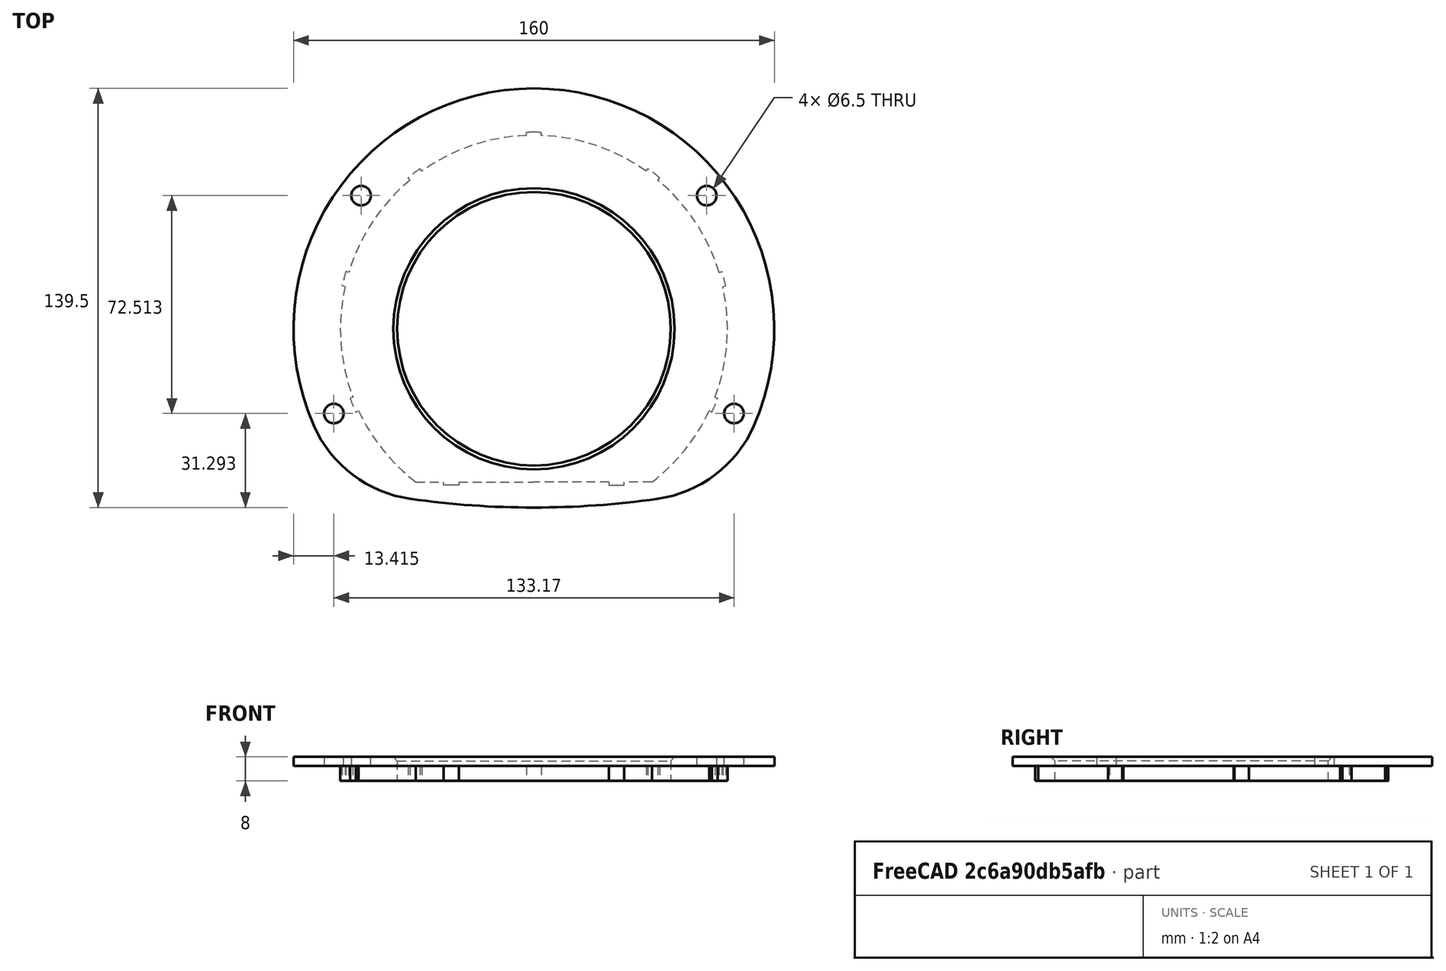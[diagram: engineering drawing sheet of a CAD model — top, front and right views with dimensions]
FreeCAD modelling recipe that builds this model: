
FCSTD DOCUMENT  (FreeCAD 0.20R29410 (Git))
Label: RevolverHole
License: All rights reserved
LicenseURL: http://en.wikipedia.org/wiki/All_rights_reserved
objects: Sketcher::SketchObject×3, PartDesign::Pad×2, Mesh::Feature×1, PartDesign::Pocket×1, PartDesign::Mirrored×1, PartDesign::Chamfer×1, PartDesign::Body×1
note: 13 computed .brp shape members not serialized (recipe doc carries the construction recipe); baked Part::Feature solids carry a one-line shape summary decoded from their .brp

FEATURE [Mesh::Feature] Revolver_Hole
FEATURE [Sketcher::SketchObject] Sketch
  FullyConstrained = true
  MapMode = 5
  Support = -> [XY_Plane]
  sketch-geometry (4):
    g0: ArcOfCircle CenterX=0 CenterY=233.5 CenterZ=0 NormalX=0 NormalY=0 NormalZ=1 AngleXU=0 Radius=293 StartAngle=4.71239 EndAngle=4.85294
    g1: ArcOfCircle CenterX=35.2333 CenterY=-15.5198 CenterZ=0 NormalX=0 NormalY=0 NormalZ=1 AngleXU=0 Radius=41.5 StartAngle=4.85294 EndAngle=5.86827
    g2: ArcOfCircle CenterX=0 CenterY=0 CenterZ=0 NormalX=0 NormalY=0 NormalZ=1 AngleXU=0 Radius=80 StartAngle=5.86827 EndAngle=7.85398
    g3: LineSegment StartX=2.45e-14 StartY=80 StartZ=0 EndX=-5.38e-14 EndY=-59.5 EndZ=0
  constraints (12):
    c: PointOnObject(g0,g-2)
    c: PointOnObject(g0,g-2)
    c: Coincident(g2,g-1)
    c: PointOnObject(g2,g-2)
    c: Coincident(g3,g2)
    c: Coincident(g3,g0)
    c: Tangent(g2,g1) = -1.5708
    c: Tangent(g1,g0) = -1.5708
    c: Diameter(g2) = 160
    c: Diameter(g0) = 586
    c: DistanceY(g0) = -59.5
    c: Diameter(g1) = 83
FEATURE [Sketcher::SketchObject] Sketch001
  FullyConstrained = true
  MapMode = 5
  Support = -> [XY_Plane]
  sketch-geometry (33):
    g0: ArcOfCircle CenterX=0 CenterY=0 CenterZ=0 NormalX=0 NormalY=0 NormalZ=1 AngleXU=0 Radius=64.4 StartAngle=5.36796 EndAngle=5.84522
    g1: LineSegment StartX=39.2589 StartY=-51.05 StartZ=0 EndX=30 EndY=-51.05 EndZ=0
    g2: LineSegment StartX=0 StartY=-51.05 StartZ=0 EndX=4e-15 EndY=65.4 EndZ=0
    g3: ArcOfCircle CenterX=0 CenterY=0 CenterZ=0 NormalX=0 NormalY=0 NormalZ=1 AngleXU=0 Radius=65.4 StartAngle=0.875886 EndAngle=0.952357
    g4: ArcOfCircle CenterX=0 CenterY=0 CenterZ=0 NormalX=0 NormalY=0 NormalZ=1 AngleXU=0 Radius=65.4 StartAngle=1.53256 EndAngle=1.5708
    g5: ArcOfCircle CenterX=0 CenterY=0 CenterZ=0 NormalX=0 NormalY=0 NormalZ=1 AngleXU=0 Radius=65.4 StartAngle=0.218961 EndAngle=0.295432
    g6: ArcOfCircle CenterX=0 CenterY=0 CenterZ=0 NormalX=0 NormalY=0 NormalZ=1 AngleXU=0 Radius=65.4 StartAngle=5.84522 EndAngle=5.92169
    g7: LineSegment StartX=59.2274 StartY=-27.7359 StartZ=0 EndX=58.3217 EndY=-27.3118 EndZ=0
    g8: LineSegment StartX=60.2378 StartY=-22.7764 StartZ=0 EndX=61.1732 EndY=-23.1301 EndZ=0
    g9: LineSegment StartX=62.8624 StartY=13.9887 StartZ=0 EndX=63.8385 EndY=14.2059 EndZ=0
    g10: LineSegment StartX=61.61 StartY=18.7503 StartZ=0 EndX=62.5666 EndY=19.0414 EndZ=0
    g11: LineSegment StartX=41.2364 StartY=49.4663 StartZ=0 EndX=41.8767 EndY=50.2345 EndZ=0
    g12: LineSegment StartX=37.3368 StartY=52.4721 StartZ=0 EndX=37.9166 EndY=53.2869 EndZ=0
    g13: LineSegment StartX=2.46177 StartY=64.3529 StartZ=0 EndX=2.5 EndY=65.3522 EndZ=0
    g14: ArcOfCircle CenterX=0 CenterY=0 CenterZ=0 NormalX=0 NormalY=0 NormalZ=1 AngleXU=0 Radius=64.4 StartAngle=0.952357 EndAngle=1.53256
    g15: ArcOfCircle CenterX=0 CenterY=0 CenterZ=0 NormalX=0 NormalY=0 NormalZ=1 AngleXU=0 Radius=64.4 StartAngle=0.295432 EndAngle=0.875886
    g16: ArcOfCircle CenterX=0 CenterY=0 CenterZ=0 NormalX=0 NormalY=0 NormalZ=1 AngleXU=0 Radius=64.4 StartAngle=5.92169 EndAngle=6.50215
    g17: LineSegment StartX=30 StartY=-52.05 StartZ=0 EndX=30 EndY=-51.05 EndZ=0
    g18: LineSegment StartX=25 StartY=-51.05 StartZ=0 EndX=25 EndY=-52.05 EndZ=0
    g19: LineSegment StartX=25 StartY=-51.05 StartZ=0 EndX=0 EndY=-51.05 EndZ=0
    g20: LineSegment StartX=41.8767 StartY=50.2345 StartZ=0 EndX=39.8967 EndY=51.7607 EndZ=0
    g21: LineSegment StartX=39.8967 StartY=51.7607 StartZ=0 EndX=37.9166 EndY=53.2869 EndZ=0
    g22: LineSegment StartX=63.8385 StartY=14.2059 StartZ=0 EndX=63.2026 EndY=16.6237 EndZ=0
    g23: LineSegment StartX=63.2026 StartY=16.6237 StartZ=0 EndX=62.5666 EndY=19.0414 EndZ=0
    g24: LineSegment StartX=59.2274 StartY=-27.7359 StartZ=0 EndX=60.2003 EndY=-25.433 EndZ=0
    g25: LineSegment StartX=60.2003 StartY=-25.433 StartZ=0 EndX=61.1732 EndY=-23.1301 EndZ=0
    g26: LineSegment StartX=4e-15 StartY=65.4 StartZ=0 EndX=39.8967 EndY=51.7607 EndZ=0
    g27: LineSegment StartX=39.8967 StartY=51.7607 StartZ=0 EndX=63.2026 EndY=16.6237 EndZ=0
    g28: LineSegment StartX=63.2026 StartY=16.6237 StartZ=0 EndX=60.2003 EndY=-25.433 EndZ=0
    g29: LineSegment StartX=2.5 StartY=65.3522 StartZ=0 EndX=0 EndY=65.3522 EndZ=0
    g30: LineSegment StartX=25 StartY=-52.05 StartZ=0 EndX=27.5 EndY=-52.05 EndZ=0
    g31: LineSegment StartX=27.5 StartY=-52.05 StartZ=0 EndX=30 EndY=-52.05 EndZ=0
    g32: LineSegment StartX=27.5 StartY=-52.05 StartZ=0 EndX=60.2003 EndY=-25.433 EndZ=0
  constraints (93):
    c: Coincident(g0,g-1)
    c: PointOnObject(g2,g-2)
    c: Coincident(g1,g0)
    c: PointOnObject(g19,g-2)
    c: Horizontal(g1)
    c: Coincident(g2,g19)
    c: Coincident(g3,g0)
    c: Coincident(g4,g0)
    c: Coincident(g5,g0)
    c: Coincident(g6,g0)
    c: Equal(g4,g3)
    c: Equal(g3,g5)
    c: Equal(g5,g6)
    c: Coincident(g7,g6)
    c: Coincident(g8,g6)
    c: Coincident(g10,g5)
    c: Coincident(g11,g3)
    c: Coincident(g12,g3)
    c: Coincident(g13,g4)
    c: Coincident(g14,g13)
    c: Equal(g0,g14)
    c: Coincident(g15,g11)
    c: Coincident(g14,g12)
    c: Coincident(g0,g14)
    c: Equal(g0,g15)
    c: Coincident(g16,g9)
    c: Coincident(g15,g10)
    c: Coincident(g0,g15)
    c: Equal(g0,g16)
    c: Coincident(g0,g7)
    c: Coincident(g16,g8)
    c: Coincident(g0,g16)
    c: Coincident(g31,g17)
    c: Coincident(g18,g30)
    c: Vertical(g17)
    c: Vertical(g18)
    c: Coincident(g1,g17)
    c: Coincident(g24,g6)
    c: Coincident(g25,g6)
    c: Coincident(g22,g5)
    c: Coincident(g20,g3)
    c: Coincident(g21,g3)
    c: DistanceX(g4) = 2.5
    c: PointOnObject(g0,g13)
    c: Coincident(g2,g4)
    c: Coincident(g20,g21)
    c: Coincident(g22,g23)
    c: Coincident(g24,g25)
    c: Equal(g24,g25)
    c: Parallel(g24,g25)
    c: Equal(g22,g23)
    c: Parallel(g22,g23)
    c: Parallel(g20,g21)
    c: Equal(g20,g21)
    c: Coincident(g26,g2)
    c: Coincident(g26,g20)
    c: Coincident(g27,g20)
    c: Coincident(g27,g22)
    c: Coincident(g28,g22)
    c: Coincident(g28,g24)
    c: Equal(g28,g27)
    c: Equal(g27,g26)
    c: PointOnObject(g0,g7)
    c: PointOnObject(g0,g8)
    c: PointOnObject(g0,g9)
    c: PointOnObject(g0,g10)
    c: PointOnObject(g0,g11)
    c: PointOnObject(g0,g12)
    c: Equal(g25,g23)
    c: Equal(g23,g21)
    c: Coincident(g29,g4)
    c: PointOnObject(g29,g-2)
    c: Horizontal(g29)
    c: Equal(g29,g21)
    c: Coincident(g18,g19)
    c: Tangent(g1,g19)
    c: Coincident(g23,g5)
    c: Coincident(g5,g9)
    c: Coincident(g30,g31)
    c: Horizontal(g30)
    c: Horizontal(g31)
    c: Distance(g30,g31) = 5
    c: Equal(g31,g30)
    c: Coincident(g32,g30)
    c: Coincident(g32,g24)
    c: Equal(g32,g28)
    c: Equal(g18,g13)
    c: Distance(g13) = 1
    c: DistanceY(g2,g2) = 116.45
    c: Diameter(g4) = 130.8
    c: DistanceY(g30,g2) = 117.45
    c: Distance(g32) = 42.1637  'L'
    c: DistanceX(g18) = 25
FEATURE [Sketcher::SketchObject] Sketch002
  FullyConstrained = true
  MapMode = 5
  Support = -> [XY_Plane]
  sketch-geometry (3):
    g0: Circle CenterX=0 CenterY=0 CenterZ=0 NormalX=0 NormalY=0 NormalZ=1 AngleXU=0 Radius=45.5
    g1: Circle CenterX=57.497 CenterY=44.3064 CenterZ=0 NormalX=0 NormalY=0 NormalZ=1 AngleXU=0 Radius=3.25
    g2: Circle CenterX=66.5848 CenterY=-28.2067 CenterZ=0 NormalX=0 NormalY=0 NormalZ=1 AngleXU=0 Radius=3.25
  constraints (8):
    c: Coincident(g0,g-1)
    c: Diameter(g0) = 91
    c: Diameter(g2) = 6.5
    c: DistanceX(g2) = 66.5848
    c: DistanceY(g2) = -28.2067
    c: Equal(g2,g1)
    c: DistanceX(g1) = 57.497
    c: DistanceY(g1) = 44.3064
FEATURE [PartDesign::Pad] Pad
  Direction = (0,0,1)
  Length = 3
  Length2 = 10
  Profile = -> Sketch
  ReferenceAxis = -> Sketch [N_Axis]
  Type = 0
FEATURE [PartDesign::Pad] Pad001
  BaseFeature = -> Pad
  Direction = (0,0,1)
  Length = 5
  Length2 = 10
  Profile = -> Sketch001
  ReferenceAxis = -> Sketch001 [N_Axis]
  Reversed = true
  Type = 0
FEATURE [PartDesign::Pocket] Pocket
  BaseFeature = -> Pad001
  Direction = (0,0,-1)
  Length = 5
  Length2 = 5
  Midplane = true
  Profile = -> Sketch002
  ReferenceAxis = -> Sketch002 [N_Axis]
  Type = 1
FEATURE [PartDesign::Mirrored] Mirrored
  BaseFeature = -> Pocket
  MirrorPlane = -> Sketch [V_Axis]
  Originals = -> [Pad,Pad001,Pocket]
FEATURE [PartDesign::Chamfer] Chamfer
  Angle = 45
  Base = -> Mirrored [Edge140]
  BaseFeature = -> Mirrored
  ChamferType = 0
  FlipDirection = false
  Size = 1.3
  Size2 = 1
  SupportTransform = false
  UseAllEdges = false
FEATURE [PartDesign::Body] Body
  Group = -> [Sketch,Sketch001,Sketch002,Pad,Pad001,Pocket,Mirrored,Chamfer]
  Origin = -> Origin
  Tip = -> Chamfer
